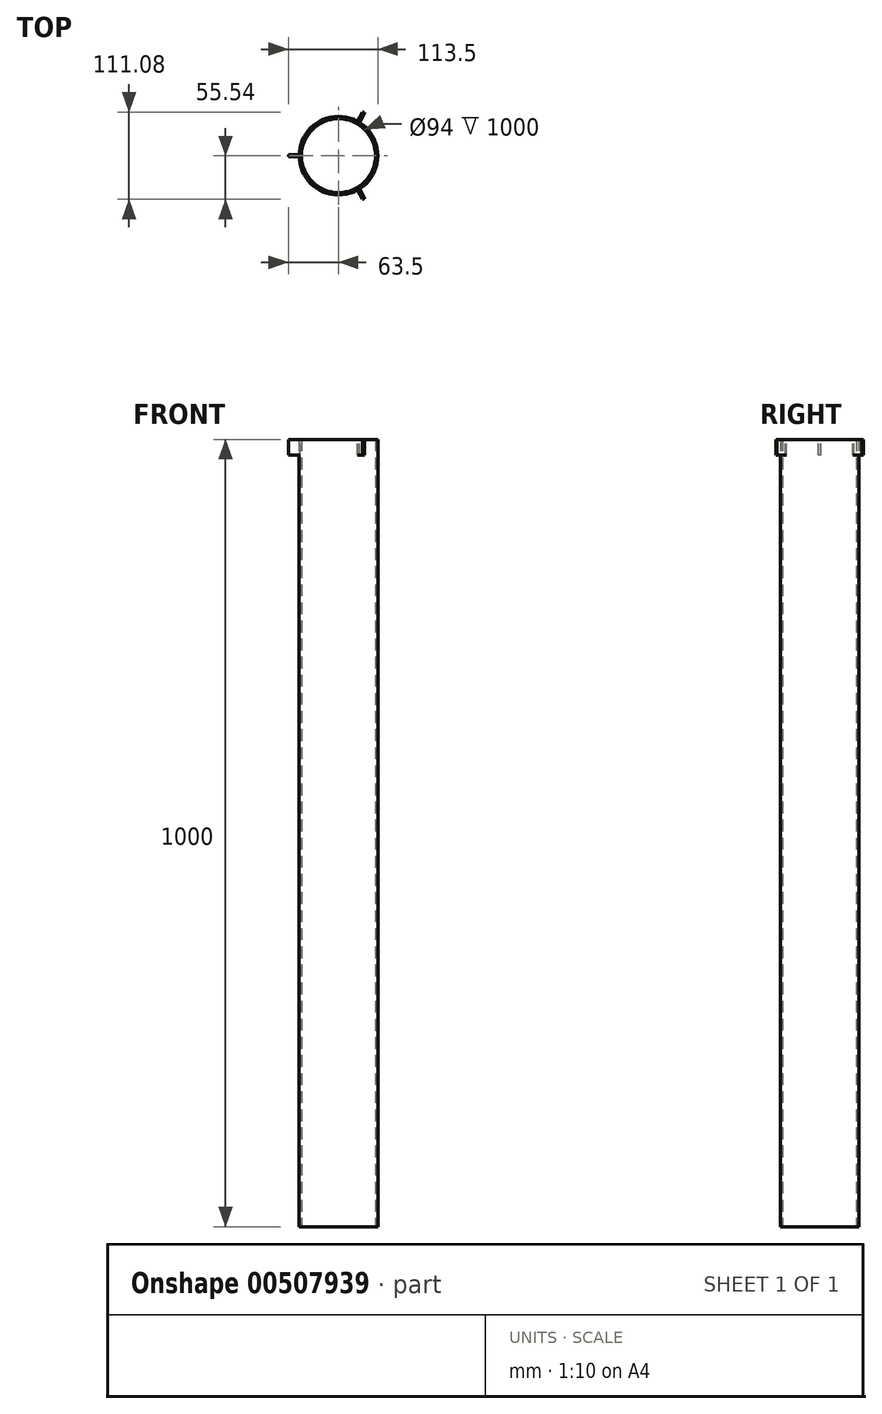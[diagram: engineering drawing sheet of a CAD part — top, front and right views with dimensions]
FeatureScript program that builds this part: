
annotation { "Feature Type Name" : "Feature", "Feature Type Description" : "" }
export const myFeature = defineFeature(function(context is Context, id is Id, definition is map)
    precondition{}
    {
        {
            var Q0;
            Q0=qCreatedBy(makeId("Front.planeOp"),FACE);
            var sketch = newSketch(context, id + "F0", { "sketchPlane" : qUnion([Q0])});
            skLineSegment(sketch, "E0", {"start": v(0.45, 2.22) * mm, "end": v(0.45, 1084.65) * mm});
            skSolve(sketch);
        }
        {
            var Q0;
            Q0=qCreatedBy(makeId("Top.planeOp"),FACE);
            var sketch = newSketch(context, id + "F1", { "sketchPlane" : qUnion([Q0])});
            skCircle(sketch, "E1", {"center": v(0, 0) * mm, "radius": 47 * mm});
            skCircle(sketch, "E2.0", {"center": v(0, 0) * mm, "radius": 50 * mm});
            skSolve(sketch);
        }
        {
            var Q0;
            Q0=qSketchRegion(id+"F1",true);
            extrude(context, id + "F2", {"entities" : qUnion([Q0]), "depth" : 1000 * mm});
        }
        {
            var Q0;
            Q0=qCreatedBy(makeId("Top.planeOp"),FACE);
            cPlane(context, id + "F3", {"entities" : qUnion([Q0]), "cplaneType" : CPlaneType.OFFSET, "offset" : 1000 * mm, "width" : 150 * mm, "height" : 150 * mm});
        }
        {
            var Q0;
            Q0=qCreatedBy(id+"F3.planeOp",FACE);
            var sketch = newSketch(context, id + "F4", { "sketchPlane" : qUnion([Q0])});
            skLineSegment(sketch, "E3.bottom", {"start": v(-49, 1.5) * mm, "end": v(-64, 1.5) * mm});
            skLineSegment(sketch, "E3.top", {"start": v(-49, -1.5) * mm, "end": v(-64, -1.5) * mm});
            skLineSegment(sketch, "E3.left", {"start": v(-49, 1.5) * mm, "end": v(-49, -1.5) * mm});
            skLineSegment(sketch, "E3.right", {"start": v(-64, 1.5) * mm, "end": v(-64, -1.5) * mm});
            skPoint(sketch, "E3.middle", {"position": v(-56.5, 0) * mm});
            skSolve(sketch);
        }
        {
            var Q0;
            Q0=qSketchRegion(id+"F4",true);
            extrude(context, id + "F5", {"entities" : qUnion([Q0]), "oppositeDirection" : true, "depth" : 20 * mm});
        }
        {
            var Q0;
            Q0=makeQuery(id+"F5.opExtrude","SWEPT_BODY",BODY,{"disambiguationData":[OSD([sQuery(id+"F4.wireOp",EDGE,"E3.bottom"),sQuery(id+"F4.wireOp",EDGE,"E3.top"),sQuery(id+"F4.wireOp",EDGE,"E3.left"),sQuery(id+"F4.wireOp",EDGE,"E3.right")])]});
            var Q1;
            Q1=sQuery(id+"F0.wireOp",EDGE,"E0");
            circularPattern(context, id + "F6", {"entities" : qUnion([Q0]), "axis" : qUnion([Q1]), "angle" : 360 * degree, "instanceCount" : 3, "equalSpace" : true});
        }
        {
            var Q0;
            Q0=qCreatedBy(id+"F3.planeOp",FACE);
            var sketch = newSketch(context, id + "F7", { "sketchPlane" : qUnion([Q0])});
            skCircle(sketch, "E4", {"center": v(0, 0) * mm, "radius": 63.5 * mm});
            skCircle(sketch, "E5.0", {"center": v(0, 0) * mm, "radius": 66.5 * mm});
            skSolve(sketch);
        }
        {
            var Q0;
            Q0=makeQuery(id+"F7.imprint","IMPRINT",FACE,{"disambiguationData":[TD([[makeQuery(id+"F7.imprint","IMPRINT",EDGE,{"derivedFrom":sQuery(id+"F7.wireOp",EDGE,"E4")}),-1.0]])]});
            extrude(context, id + "F8", {"entities" : qUnion([Q0]), "operationType" : NewBodyOperationType.REMOVE, "oppositeDirection" : true, "depth" : 20 * mm});
        }
    });
